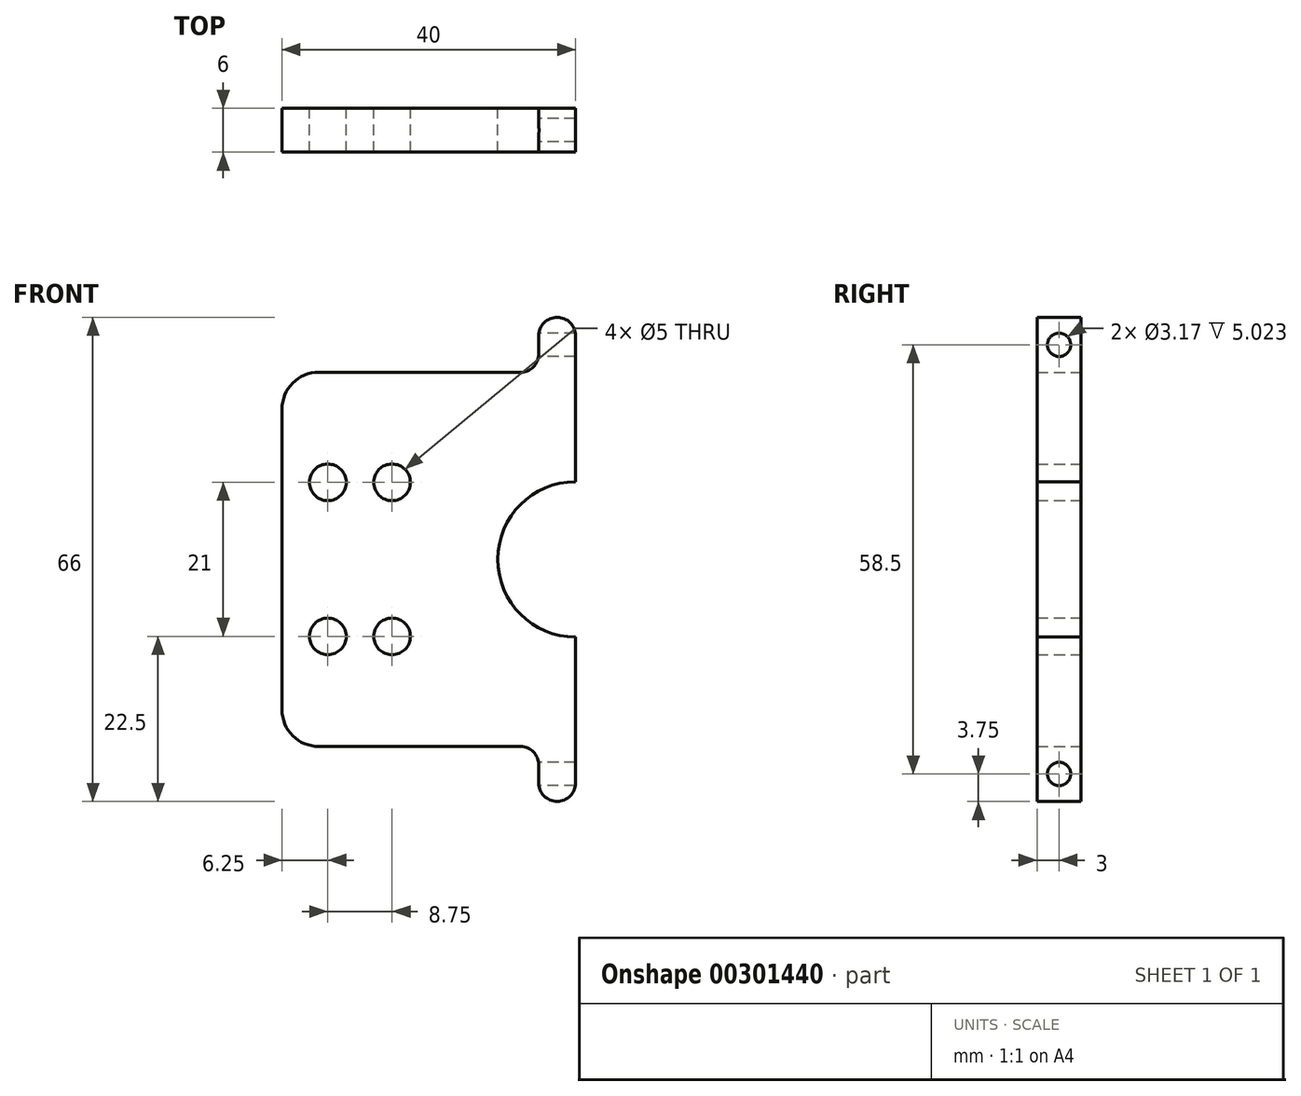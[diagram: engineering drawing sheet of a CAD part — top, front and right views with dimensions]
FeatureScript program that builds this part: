
annotation { "Feature Type Name" : "Feature", "Feature Type Description" : "" }
export const myFeature = defineFeature(function(context is Context, id is Id, definition is map)
    precondition{}
    {
        {
            var Q0;
            Q0=qCreatedBy(makeId("Front.planeOp"),FACE);
            var sketch = newSketch(context, id + "F0", { "sketchPlane" : qUnion([Q0])});
            skPoint(sketch, "E0", {"position": v(-29.1, 8.76) * mm});
            skCircle(sketch, "E1", {"center": v(-22.85, 8.76) * mm, "radius": 2.5 * mm});
            skCircle(sketch, "E2", {"center": v(-14.1, 8.76) * mm, "radius": 2.5 * mm});
            skCircle(sketch, "E3.MirrorC", {"center": v(-22.85, -12.24) * mm, "radius": 2.5 * mm});
            skCircle(sketch, "E4.MirrorC", {"center": v(-14.1, -12.24) * mm, "radius": 2.5 * mm});
            skLineSegment(sketch, "E5", {"start": v(-29.1, 8.76) * mm, "end": v(-14.1, 8.76) * mm});
            skLineSegment(sketch, "E6", {"start": v(-14.1, -12.24) * mm, "end": v(-29.1, -12.24) * mm});
            skPoint(sketch, "E7", {"position": v(5.9, 23.76) * mm});
            skPoint(sketch, "E8.MirrorP", {"position": v(5.9, -27.24) * mm});
            skPoint(sketch, "E9", {"position": v(10.9, 31.26) * mm});
            skLineSegment(sketch, "E10", {"start": v(10.9, -27.24) * mm, "end": v(10.9, -34.74) * mm});
            skLineSegment(sketch, "E11", {"start": v(10.9, 23.76) * mm, "end": v(10.9, 8.85) * mm});
            skArc(sketch, "E12", {"start": v(10.9, 8.85) * mm, "mid": v(0.31, -1.74) * mm, "end": v(10.9, -12.33) * mm});
            skLineSegment(sketch, "E13", {"start": v(10.9, -12.33) * mm, "end": v(10.9, -27.24) * mm});
            skLineSegment(sketch, "E14", {"start": v(10.9, 23.76) * mm, "end": v(10.9, 27.5) * mm});
            skLineSegment(sketch, "E15", {"start": v(10.9, -32.24) * mm, "end": v(10.9, -30.99) * mm});
            skLineSegment(sketch, "E16", {"start": v(3.4, -27.24) * mm, "end": v(3.4, -27.24) * mm});
            skArc(sketch, "E17.filletArc", {"start": v(5.9, -29.74) * mm, "mid": v(5.17, -27.97) * mm, "end": v(3.4, -27.24) * mm});
            skLineSegment(sketch, "E18", {"start": v(5.9, -32.24) * mm, "end": v(5.9, -32.24) * mm});
            skLineSegment(sketch, "E19", {"start": v(8.4, -34.74) * mm, "end": v(8.4, -34.74) * mm});
            skLineSegment(sketch, "E20", {"start": v(10.9, -34.74) * mm, "end": v(10.9, -32.24) * mm});
            skLineSegment(sketch, "E21", {"start": v(5.9, -29.74) * mm, "end": v(5.9, -32.24) * mm});
            skPoint(sketch, "E22.visualSharp", {"position": v(5.9, -34.74) * mm});
            skArc(sketch, "E22.filletArc", {"start": v(5.9, -32.24) * mm, "mid": v(6.63, -34) * mm, "end": v(8.4, -34.74) * mm});
            skPoint(sketch, "E23.visualSharp", {"position": v(10.9, -34.74) * mm});
            skArc(sketch, "E23.filletArc", {"start": v(8.4, -34.74) * mm, "mid": v(10.17, -34) * mm, "end": v(10.9, -32.24) * mm});
            skArc(sketch, "E24.MirrorCS", {"start": v(5.9, 26.26) * mm, "mid": v(5.17, 24.5) * mm, "end": v(3.4, 23.76) * mm});
            skLineSegment(sketch, "E25.MirrorCS", {"start": v(5.9, 26.26) * mm, "end": v(5.9, 28.76) * mm});
            skArc(sketch, "E26.MirrorCS", {"start": v(5.9, 28.76) * mm, "mid": v(6.63, 30.53) * mm, "end": v(8.4, 31.26) * mm});
            skArc(sketch, "E27.MirrorCS", {"start": v(8.4, 31.26) * mm, "mid": v(10.17, 30.53) * mm, "end": v(10.9, 28.76) * mm});
            skLineSegment(sketch, "E28.MirrorCS", {"start": v(10.9, 28.76) * mm, "end": v(10.9, 27.5) * mm});
            skLineSegment(sketch, "E29", {"start": v(-24.1, 23.76) * mm, "end": v(3.4, 23.76) * mm});
            skPoint(sketch, "E30.visualSharp", {"position": v(-29.1, 23.76) * mm});
            skArc(sketch, "E30.filletArc", {"start": v(-24.1, 23.76) * mm, "mid": v(-27.64, 22.3) * mm, "end": v(-29.1, 18.76) * mm});
            skArc(sketch, "E31.MirrorCS", {"start": v(-24.1, -27.24) * mm, "mid": v(-27.64, -25.78) * mm, "end": v(-29.1, -22.24) * mm});
            skLineSegment(sketch, "E32", {"start": v(-24.1, -27.24) * mm, "end": v(3.4, -27.24) * mm});
            skLineSegment(sketch, "E33", {"start": v(-29.1, -22.24) * mm, "end": v(-29.1, 18.76) * mm});
            skSolve(sketch);
        }
        {
            var Q0;
            Q0=makeQuery(id+"F0.imprint","IMPRINT",FACE,{"disambiguationData":[TD([[makeQuery(id+"F0.imprint","IMPRINT",EDGE,{"derivedFrom":sQuery(id+"F0.wireOp",EDGE,"E2")}),-1.0]])]});
            extrude(context, id + "F1", {"entities" : qUnion([Q0]), "endBound" : BoundingType.SYMMETRIC, "depth" : 6 * mm});
        }
        {
            var Q0;
            Q0=qCreatedBy(makeId("Right.planeOp"),FACE);
            var sketch = newSketch(context, id + "F2", { "sketchPlane" : qUnion([Q0])});
            skCircle(sketch, "E34", {"center": v(0, 27.5) * mm, "radius": 1.59 * mm});
            skCircle(sketch, "E35", {"center": v(0, -30.99) * mm, "radius": 1.59 * mm});
            skSolve(sketch);
        }
        {
            var Q0;
            Q0 = qSketchRegion(id + "F2", true);
            extrude(context, id + "F3", {"entities" : qUnion([Q0]), "operationType" : NewBodyOperationType.REMOVE, "endBound" : BoundingType.THROUGH_ALL, "depth" : 25 * mm});
        }
    });
